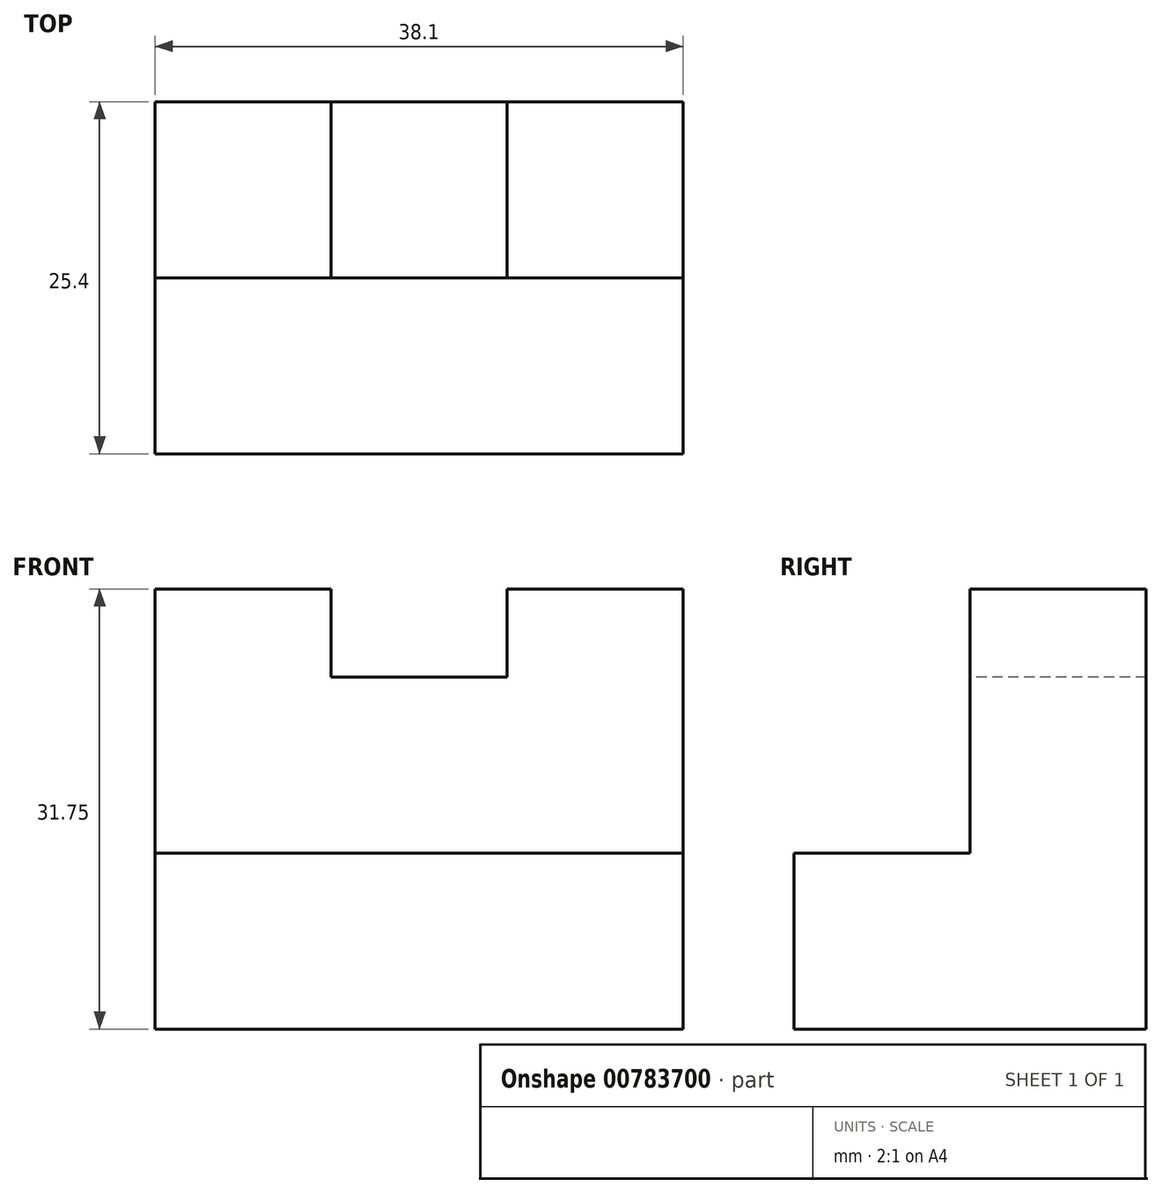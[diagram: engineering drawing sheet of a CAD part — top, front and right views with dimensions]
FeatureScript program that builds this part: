
annotation { "Feature Type Name" : "Feature", "Feature Type Description" : "" }
export const myFeature = defineFeature(function(context is Context, id is Id, definition is map)
    precondition{}
    {
        {
            var Q0;
            Q0=qCreatedBy(makeId("Right.planeOp"),FACE);
            var sketch = newSketch(context, id + "F0", { "sketchPlane" : qUnion([Q0])});
            skLineSegment(sketch, "E0", {"start": v(0, 0) * mm, "end": v(25.4, 0) * mm});
            skLineSegment(sketch, "E1", {"start": v(25.4, 0) * mm, "end": v(25.4, 31.75) * mm});
            skLineSegment(sketch, "E2", {"start": v(25.4, 31.75) * mm, "end": v(0, 31.75) * mm});
            skLineSegment(sketch, "E3", {"start": v(0, 31.75) * mm, "end": v(0, 0) * mm});
            skSolve(sketch);
        }
        {
            var Q0;
            Q0=makeQuery(id+"F0.imprint","IMPRINT",FACE,{"disambiguationData":[TD([[makeQuery(id+"F0.imprint","IMPRINT",EDGE,{"derivedFrom":sQuery(id+"F0.wireOp",EDGE,"E0")}),1.0]])]});
            extrude(context, id + "F1", {"entities" : qUnion([Q0]), "depth" : 25.4 * mm, "offsetDistance" : 25.4 * mm});
        }
        {
            var Q0;
            Q0=makeQuery(id+"F1.opExtrude","CAP_FACE",FACE,{"disambiguationData":[OSD([sQuery(id+"F0.wireOp",EDGE,"E0"),sQuery(id+"F0.wireOp",EDGE,"E1"),sQuery(id+"F0.wireOp",EDGE,"E2"),sQuery(id+"F0.wireOp",EDGE,"E3")])],"isStart":false});
            var sketch = newSketch(context, id + "F2", { "sketchPlane" : qUnion([Q0])});
            skLineSegment(sketch, "E4", {"start": v(25.4, 31.75) * mm, "end": v(12.7, 31.75) * mm});
            skLineSegment(sketch, "E5", {"start": v(12.7, 31.75) * mm, "end": v(12.7, 12.7) * mm});
            skLineSegment(sketch, "E6", {"start": v(12.7, 12.7) * mm, "end": v(0, 12.7) * mm});
            skSolve(sketch);
        }
        {
            var Q0;
            {var subQ0=sQuery(id+"F2.wireOp",EDGE,"E5");Q0=makeQuery(id+"F2.imprint","IMPRINT",FACE,{"disambiguationData":[TD([[makeQuery(id+"F2.imprint","IMPRINT",EDGE,{"derivedFrom":subQ0}),-1.0]])]});}
            extrude(context, id + "F3", {"entities" : qUnion([Q0]), "operationType" : NewBodyOperationType.REMOVE, "oppositeDirection" : true, "depth" : 25.4 * mm, "offsetDistance" : 25.4 * mm});
        }
        {
            var Q0;
            Q0=makeQuery(id+"F1.opExtrude","CAP_FACE",FACE,{"disambiguationData":[OSD([sQuery(id+"F0.wireOp",EDGE,"E0"),sQuery(id+"F0.wireOp",EDGE,"E1"),sQuery(id+"F0.wireOp",EDGE,"E2"),sQuery(id+"F0.wireOp",EDGE,"E3")])],"isStart":false});
            extrude(context, id + "F4", {"entities" : qUnion([Q0]), "operationType" : NewBodyOperationType.ADD, "depth" : 12.7 * mm, "offsetDistance" : 25.4 * mm});
        }
        {
            var Q0;
            {var subQ0=sQuery(id+"F2.wireOp",EDGE,"E5");Q0=makeQuery(id+"F4.boolean.opBoolean","MERGE",FACE,{"derivedFrom":[makeQuery(id+"F3.boolean.opBoolean","COPY",FACE,{"derivedFrom":makeQuery(id+"F3.opExtrude","SWEPT_FACE",FACE,{"disambiguationData":[OSD([subQ0])]})}),makeQuery(id+"F4.opExtrude","SWEPT_FACE",FACE,{"disambiguationData":[OSD([subQ0])]})]});}
            var sketch = newSketch(context, id + "F5", { "sketchPlane" : qUnion([Q0])});
            skLineSegment(sketch, "E7", {"start": v(0, 31.75) * mm, "end": v(12.7, 31.75) * mm});
            skLineSegment(sketch, "E8", {"start": v(12.7, 31.75) * mm, "end": v(12.7, 25.4) * mm});
            skLineSegment(sketch, "E9", {"start": v(12.7, 25.4) * mm, "end": v(25.4, 25.4) * mm});
            skLineSegment(sketch, "E10", {"start": v(25.4, 25.4) * mm, "end": v(25.4, 31.75) * mm});
            skLineSegment(sketch, "E11", {"start": v(25.4, 31.75) * mm, "end": v(38.1, 31.75) * mm});
            skSolve(sketch);
        }
        {
            var Q0;
            {var subQ0=sQuery(id+"F5.wireOp",EDGE,"E8");Q0=makeQuery(id+"F5.imprint","IMPRINT",FACE,{"disambiguationData":[TD([[makeQuery(id+"F5.imprint","IMPRINT",EDGE,{"derivedFrom":subQ0}),1.0]])]});}
            var sketch = newSketch(context, id + "F6", { "sketchPlane" : qUnion([Q0])});
            skSolve(sketch);
        }
        {
            var Q0;
            Q0 = qSketchRegion(id + "F6", true);
            var Q1;
            {var subQ0=sQuery(id+"F5.wireOp",EDGE,"E8");Q1=makeQuery(id+"F6.imprint","IMPRINT",FACE,{"disambiguationData":[TD([[makeQuery(id+"F6.imprint","IMPRINT",EDGE,{"derivedFrom":makeQuery(id+"F5.imprint","IMPRINT",EDGE,{"derivedFrom":subQ0})}),1.0]])]});}
            extrude(context, id + "F7", {"entities" : qUnion([Q0, Q1]), "operationType" : NewBodyOperationType.REMOVE, "oppositeDirection" : true, "depth" : 25.4 * mm, "offsetDistance" : 25.4 * mm});
        }
    });
